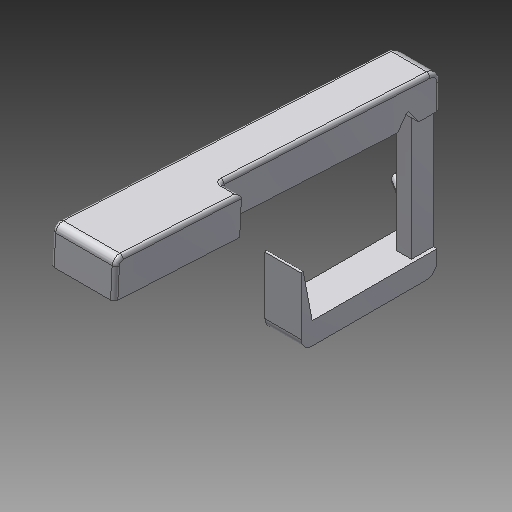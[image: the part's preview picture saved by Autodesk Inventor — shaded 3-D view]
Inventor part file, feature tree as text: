
AUTODESK INVENTOR PART (.ipt)
format: ipt  version: 2018 (Build 220112000, 112)  size: 307,200 bytes
history: native  units: mm
features: extrude x7, fillet x6, other x3, draft x1, chamfer x1
ambient origin geometry x8: Origin, YZ Plane, XZ Plane, XY Plane, X Axis, Y Axis, Z Axis, Center Point
bodies: Solid1 (feature_tree)
feature tree (18):
  other  "Key Sketch"
  extrude  "Upper Key"  Depth=10.0mm
  extrude  "Lower Key"  Depth=1.0mm
  other  "Hinge Cut Sketch"
  extrude  "Hinge Cut"  Depth=10.0mm TaperAngle=0.0deg
  extrude  "Hinge Cut 2"  Depth=3.0mm
  other  "Lever Sketch"
  extrude  "Vertical Lever"  Depth=3.0mm
  extrude  "Horizontal Lever"  Depth=33.6625mm
  extrude  "Spring Hook"  Depth=0.5mm
  draft  "FaceDraft3"
  chamfer  "Chamfer1"  Distance=3.0mm
  fillet  "Fillet9"  Radius=6.0mm
  fillet  "Fillet10"  Radius=4.0mm
  fillet  "Fillet5"  Radius=10.0mm
  fillet  "Fillet4"  [1 undecoded]
  fillet  "Fillet11"  Radius=3.0mm
  fillet  "Fillet14"  Radius=2.3mm
note: 1 required parameter value undecoded (feature->parameter linkage not recoverable at this tier; creation-order binding heuristic only, values carry confidence <= 0.55)
